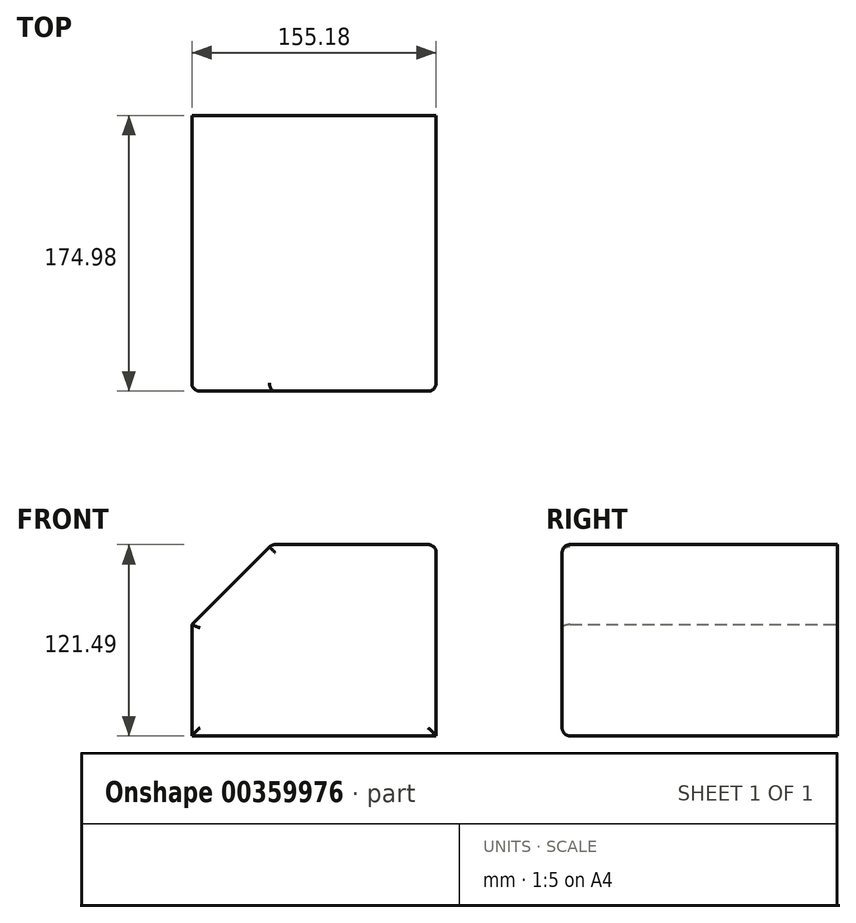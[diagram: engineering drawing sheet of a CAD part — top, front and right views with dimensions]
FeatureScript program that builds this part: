
annotation { "Feature Type Name" : "Feature", "Feature Type Description" : "" }
export const myFeature = defineFeature(function(context is Context, id is Id, definition is map)
    precondition{}
    {
        {
            var Q0;
            Q0=qCreatedBy(makeId("Front.planeOp"),FACE);
            var sketch = newSketch(context, id + "F0", { "sketchPlane" : qUnion([Q0])});
            skLineSegment(sketch, "E0.bottom", {"start": v(0, 0) * mm, "end": v(155.18, 0) * mm});
            skLineSegment(sketch, "E0.top", {"start": v(0, 121.49) * mm, "end": v(155.18, 121.49) * mm});
            skLineSegment(sketch, "E0.left", {"start": v(0, 0) * mm, "end": v(0, 121.49) * mm});
            skLineSegment(sketch, "E0.right", {"start": v(155.18, 0) * mm, "end": v(155.18, 121.49) * mm});
            skSolve(sketch);
        }
        {
            var Q0;
            Q0=makeQuery(id+"F0.imprint","IMPRINT",FACE,{"disambiguationData":[TD([[makeQuery(id+"F0.imprint","IMPRINT",EDGE,{"derivedFrom":sQuery(id+"F0.wireOp",EDGE,"E0.bottom")}),1.0]])]});
            extrude(context, id + "F1", {"entities" : qUnion([Q0]), "depth" : 174.98 * mm});
        }
        {
            var Q0;
            Q0=makeQuery(id+"F1.opExtrude","SWEPT_EDGE",EDGE,{"disambiguationData":[OSD([sQuery(id+"F0.wireOp",EDGE,"E0.top"),sQuery(id+"F0.wireOp",EDGE,"E0.left")])]});
            chamfer(context, id + "F2", {"entities" : qUnion([Q0]), "width" : 50.8 * mm, "tangentPropagation" : true});
        }
        {
            var Q0;
            {var subQ0=sQuery(id+"F0.wireOp",EDGE,"E0.left");var subQ1=sQuery(id+"F0.wireOp",EDGE,"E0.top");Q0=makeQuery(id+"F2.opChamfer","BLEND_EDGE",EDGE,{"blendedFrom":[makeQuery(id+"F1.opExtrude","SWEPT_EDGE",EDGE,{"disambiguationData":[OSD([subQ1,subQ0])]}),makeQuery(id+"F1.opExtrude","CAP_FACE",FACE,{"disambiguationData":[OSD([sQuery(id+"F0.wireOp",EDGE,"E0.bottom"),subQ1,subQ0,sQuery(id+"F0.wireOp",EDGE,"E0.right")])],"isStart":false})],"blendedInto":[makeQuery(id+"F1.opExtrude","CAP_FACE",FACE,{"disambiguationData":[OSD([sQuery(id+"F0.wireOp",EDGE,"E0.bottom"),subQ1,subQ0,sQuery(id+"F0.wireOp",EDGE,"E0.right")])],"isStart":false})]});}
            var Q1;
            Q1=makeQuery(id+"F1.opExtrude","CAP_FACE",FACE,{"disambiguationData":[OSD([sQuery(id+"F0.wireOp",EDGE,"E0.bottom"),sQuery(id+"F0.wireOp",EDGE,"E0.top"),sQuery(id+"F0.wireOp",EDGE,"E0.left"),sQuery(id+"F0.wireOp",EDGE,"E0.right")])],"isStart":false});
            var Q2;
            Q2=makeQuery(id+"F1.opExtrude","CAP_EDGE",EDGE,{"disambiguationData":[OSD([sQuery(id+"F0.wireOp",EDGE,"E0.left")])],"isStart":false});
            var Q3;
            Q3=makeQuery(id+"F1.opExtrude","CAP_EDGE",EDGE,{"disambiguationData":[OSD([sQuery(id+"F0.wireOp",EDGE,"E0.bottom")])],"isStart":false});
            var Q4;
            Q4=makeQuery(id+"F1.opExtrude","CAP_EDGE",EDGE,{"disambiguationData":[OSD([sQuery(id+"F0.wireOp",EDGE,"E0.right")])],"isStart":false});
            fillet(context, id + "F3", {"entities" : qUnion([Q0, Q1, Q2, Q3, Q4]), "tangentPropagation" : true, "radius" : 5.08 * mm, "defaultsChanged" : false, "vertexSettings" : [], "allowEdgeOverflow" : false});
        }
        {
            var Q0;
            {var subQ0=sQuery(id+"F0.wireOp",EDGE,"E0.top");var subQ1=sQuery(id+"F0.wireOp",EDGE,"E0.left");Q0=makeQuery(id+"F3.opFillet","BLEND_EDGE",EDGE,{"blendedFrom":[makeQuery(id+"F2.opChamfer","BLEND_EDGE",EDGE,{"blendedFrom":[makeQuery(id+"F1.opExtrude","SWEPT_EDGE",EDGE,{"disambiguationData":[OSD([subQ0,subQ1])]}),makeQuery(id+"F1.opExtrude","CAP_FACE",FACE,{"disambiguationData":[OSD([sQuery(id+"F0.wireOp",EDGE,"E0.bottom"),subQ0,subQ1,sQuery(id+"F0.wireOp",EDGE,"E0.right")])],"isStart":false})],"blendedInto":[makeQuery(id+"F1.opExtrude","CAP_FACE",FACE,{"disambiguationData":[OSD([sQuery(id+"F0.wireOp",EDGE,"E0.bottom"),subQ0,subQ1,sQuery(id+"F0.wireOp",EDGE,"E0.right")])],"isStart":false})]}),makeQuery(id+"F1.opExtrude","CAP_EDGE",EDGE,{"disambiguationData":[OSD([subQ0])],"isStart":false})],"blendedInto":[]});}
            var Q1;
            {var subQ0=sQuery(id+"F0.wireOp",EDGE,"E0.top");Q1=makeQuery(id+"F3.opFillet","BLEND_EDGE",EDGE,{"blendedFrom":[makeQuery(id+"F1.opExtrude","CAP_EDGE",EDGE,{"disambiguationData":[OSD([subQ0])],"isStart":false}),makeQuery(id+"F1.opExtrude","SWEPT_FACE",FACE,{"disambiguationData":[OSD([subQ0])]})],"blendedInto":[makeQuery(id+"F1.opExtrude","SWEPT_FACE",FACE,{"disambiguationData":[OSD([subQ0])]})]});}
            var Q2;
            Q2=makeQuery(id+"F3.opFillet","BLEND_EDGE",EDGE,{"blendedFrom":[makeQuery(id+"F1.opExtrude","CAP_EDGE",EDGE,{"disambiguationData":[OSD([sQuery(id+"F0.wireOp",EDGE,"E0.right")])],"isStart":false}),makeQuery(id+"F1.opExtrude","CAP_EDGE",EDGE,{"disambiguationData":[OSD([sQuery(id+"F0.wireOp",EDGE,"E0.top")])],"isStart":false})],"blendedInto":[]});
            var Q3;
            {var subQ0=sQuery(id+"F0.wireOp",EDGE,"E0.top");Q3=makeQuery(id+"F3.opFillet","BLEND_EDGE",EDGE,{"blendedFrom":[makeQuery(id+"F1.opExtrude","CAP_EDGE",EDGE,{"disambiguationData":[OSD([subQ0])],"isStart":false}),makeQuery(id+"F1.opExtrude","CAP_FACE",FACE,{"disambiguationData":[OSD([sQuery(id+"F0.wireOp",EDGE,"E0.bottom"),subQ0,sQuery(id+"F0.wireOp",EDGE,"E0.left"),sQuery(id+"F0.wireOp",EDGE,"E0.right")])],"isStart":false})],"blendedInto":[makeQuery(id+"F1.opExtrude","CAP_FACE",FACE,{"disambiguationData":[OSD([sQuery(id+"F0.wireOp",EDGE,"E0.bottom"),subQ0,sQuery(id+"F0.wireOp",EDGE,"E0.left"),sQuery(id+"F0.wireOp",EDGE,"E0.right")])],"isStart":false})]});}
            var Q4;
            Q4=makeQuery(id+"F3.opFillet","BLEND_FACE",FACE,{"disambiguationData":[OSD([sQuery(id+"F0.wireOp",EDGE,"E0.top")])]});
            fillet(context, id + "F4", {"entities" : qUnion([Q0, Q1, Q2, Q3, Q4]), "tangentPropagation" : true, "radius" : 5.08 * mm, "defaultsChanged" : false, "vertexSettings" : [], "allowEdgeOverflow" : false});
        }
    });
